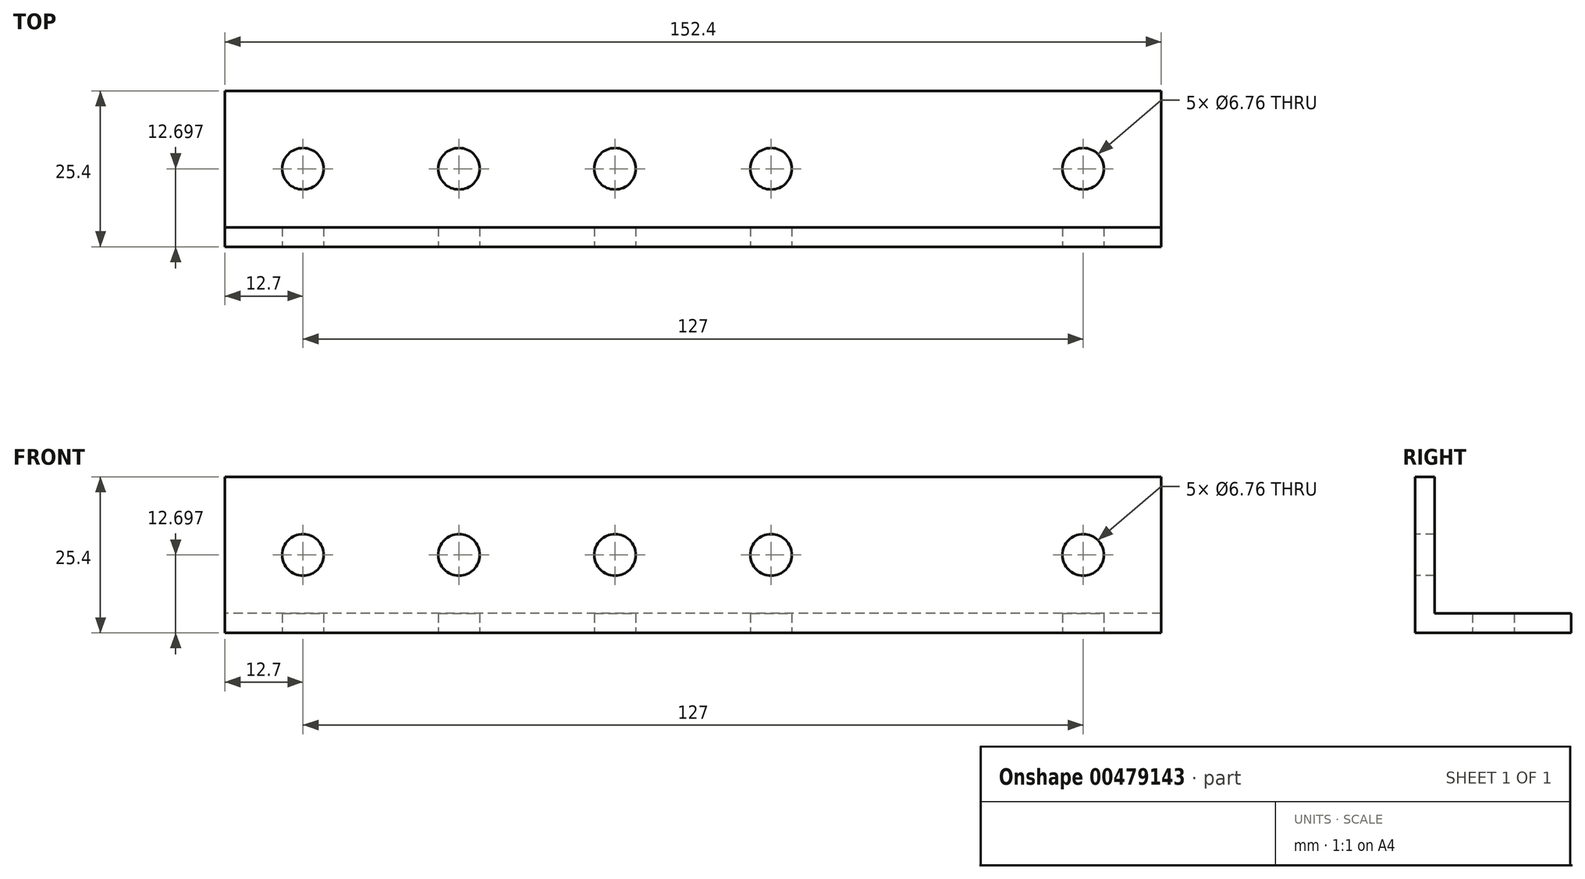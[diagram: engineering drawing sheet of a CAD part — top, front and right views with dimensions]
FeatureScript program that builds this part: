
annotation { "Feature Type Name" : "Feature", "Feature Type Description" : "" }
export const myFeature = defineFeature(function(context is Context, id is Id, definition is map)
    precondition{}
    {
        {
            var Q0;
            Q0=qCreatedBy(makeId("Right.planeOp"),FACE);
            var sketch = newSketch(context, id + "F0", { "sketchPlane" : qUnion([Q0])});
            skLineSegment(sketch, "E0", {"start": v(-59.67, 48.75) * mm, "end": v(-59.67, 23.35) * mm});
            skLineSegment(sketch, "E1", {"start": v(-59.67, 23.35) * mm, "end": v(-34.27, 23.35) * mm});
            skLineSegment(sketch, "E2", {"start": v(-34.27, 23.35) * mm, "end": v(-34.27, 26.52) * mm});
            skLineSegment(sketch, "E3", {"start": v(-34.27, 26.52) * mm, "end": v(-56.5, 26.52) * mm});
            skLineSegment(sketch, "E4", {"start": v(-56.5, 26.52) * mm, "end": v(-56.5, 48.75) * mm});
            skLineSegment(sketch, "E5", {"start": v(-56.5, 48.75) * mm, "end": v(-59.67, 48.75) * mm});
            skSolve(sketch);
        }
        {
            var Q0;
            Q0 = qSketchRegion(id + "F0", true);
            extrude(context, id + "F1", {"entities" : qUnion([Q0]), "depth" : 127 * mm});
        }
        {
            var Q0;
            Q0=makeQuery(id+"F1.opExtrude","CAP_FACE",FACE,{"disambiguationData":[OSD([sQuery(id+"F0.wireOp",EDGE,"E0"),sQuery(id+"F0.wireOp",EDGE,"E1"),sQuery(id+"F0.wireOp",EDGE,"E2"),sQuery(id+"F0.wireOp",EDGE,"E3"),sQuery(id+"F0.wireOp",EDGE,"E4"),sQuery(id+"F0.wireOp",EDGE,"E5")])],"isStart":true});
            extrude(context, id + "F2", {"entities" : qUnion([Q0]), "operationType" : NewBodyOperationType.ADD, "depth" : 25.4 * mm});
        }
        {
            var Q0;
            Q0=makeQuery(id+"F1.opExtrude","SWEPT_FACE",FACE,{"disambiguationData":[OSD([sQuery(id+"F0.wireOp",EDGE,"E0")])]});
            var sketch = newSketch(context, id + "F3", { "sketchPlane" : qUnion([Q0])});
            skPoint(sketch, "E6", {"position": v(114.3, 36.05) * mm});
            skPoint(sketch, "E6.positionSnap0", {"position": v(127, 36.05) * mm});
            skPoint(sketch, "E7", {"position": v(88.9, 36.05) * mm});
            skPoint(sketch, "E8", {"position": v(63.5, 36.05) * mm});
            skPoint(sketch, "E9", {"position": v(38.1, 36.05) * mm});
            skPoint(sketch, "E10", {"position": v(12.7, 36.05) * mm});
            skPoint(sketch, "E11", {"position": v(-12.7, 36.05) * mm});
            skPoint(sketch, "E12", {"position": v(-38.1, 36.05) * mm});
            skSolve(sketch);
        }
        {
            var Q0;
            Q0=makeQuery(id+"F1.opExtrude","SWEPT_FACE",FACE,{"disambiguationData":[OSD([sQuery(id+"F0.wireOp",EDGE,"E1")])]});
            var sketch = newSketch(context, id + "F4", { "sketchPlane" : qUnion([Q0])});
            skPoint(sketch, "E13", {"position": v(114.3, 46.97) * mm});
            skPoint(sketch, "E13.positionSnap0", {"position": v(127, 46.97) * mm});
            skPoint(sketch, "E14", {"position": v(88.9, 46.97) * mm});
            skPoint(sketch, "E15", {"position": v(63.5, 46.97) * mm});
            skPoint(sketch, "E16", {"position": v(12.7, 46.97) * mm});
            skPoint(sketch, "E17", {"position": v(38.1, 46.97) * mm});
            skPoint(sketch, "E18", {"position": v(-12.7, 46.97) * mm});
            skPoint(sketch, "E19", {"position": v(-38.1, 46.97) * mm});
            skSolve(sketch);
        }
        {
            var Q0;
            Q0=sQuery(id+"F4.wireOp",VERTEX,"E13");
            var Q1;
            Q1=sQuery(id+"F3.wireOp",VERTEX,"E6");
            var Q2;
            Q2=sQuery(id+"F4.wireOp",VERTEX,"E15");
            var Q3;
            Q3=sQuery(id+"F3.wireOp",VERTEX,"E8");
            var Q4;
            Q4=sQuery(id+"F4.wireOp",VERTEX,"E17");
            var Q5;
            Q5=sQuery(id+"F3.wireOp",VERTEX,"E9");
            var Q6;
            Q6=sQuery(id+"F3.wireOp",VERTEX,"E10");
            var Q7;
            Q7=sQuery(id+"F4.wireOp",VERTEX,"E16");
            var Q8;
            Q8=sQuery(id+"F3.wireOp",VERTEX,"E11");
            var Q9;
            Q9=sQuery(id+"F4.wireOp",VERTEX,"E18");
            var Q10;
            Q10=makeQuery(id+"F1.opExtrude","SWEPT_BODY",BODY,{"disambiguationData":[OSD([sQuery(id+"F0.wireOp",EDGE,"E0"),sQuery(id+"F0.wireOp",EDGE,"E1"),sQuery(id+"F0.wireOp",EDGE,"E2"),sQuery(id+"F0.wireOp",EDGE,"E3"),sQuery(id+"F0.wireOp",EDGE,"E4"),sQuery(id+"F0.wireOp",EDGE,"E5")])]});
            hole(context, id + "F5", {"style" : HoleStyle.SIMPLE, "endStyle" : HoleEndStyle.BLIND, "standardTappedOrClearance" : lookupTablePath({ "standard" : "ANSI", "fit" : "Normal (ASME)", "size" : "1/4", "type" : "Clearance" }), "standardBlindInLast" : lookupTablePath({ "fit" : "Free", "standard" : "ANSI", "size" : "1/4", "type" : "Clearance" }), "holeDiameter" : 6.76 * mm, "holeDepth" : 76.2 * mm, "isTappedThrough" : true, "tappedDepth" : 12.7 * mm, "tapClearance" : 3, "startFromSketch" : true, "locations" : qUnion([Q0, Q1, Q2, Q3, Q4, Q5, Q6, Q7, Q8, Q9]), "scope" : qUnion([Q10])});
        }
    });
